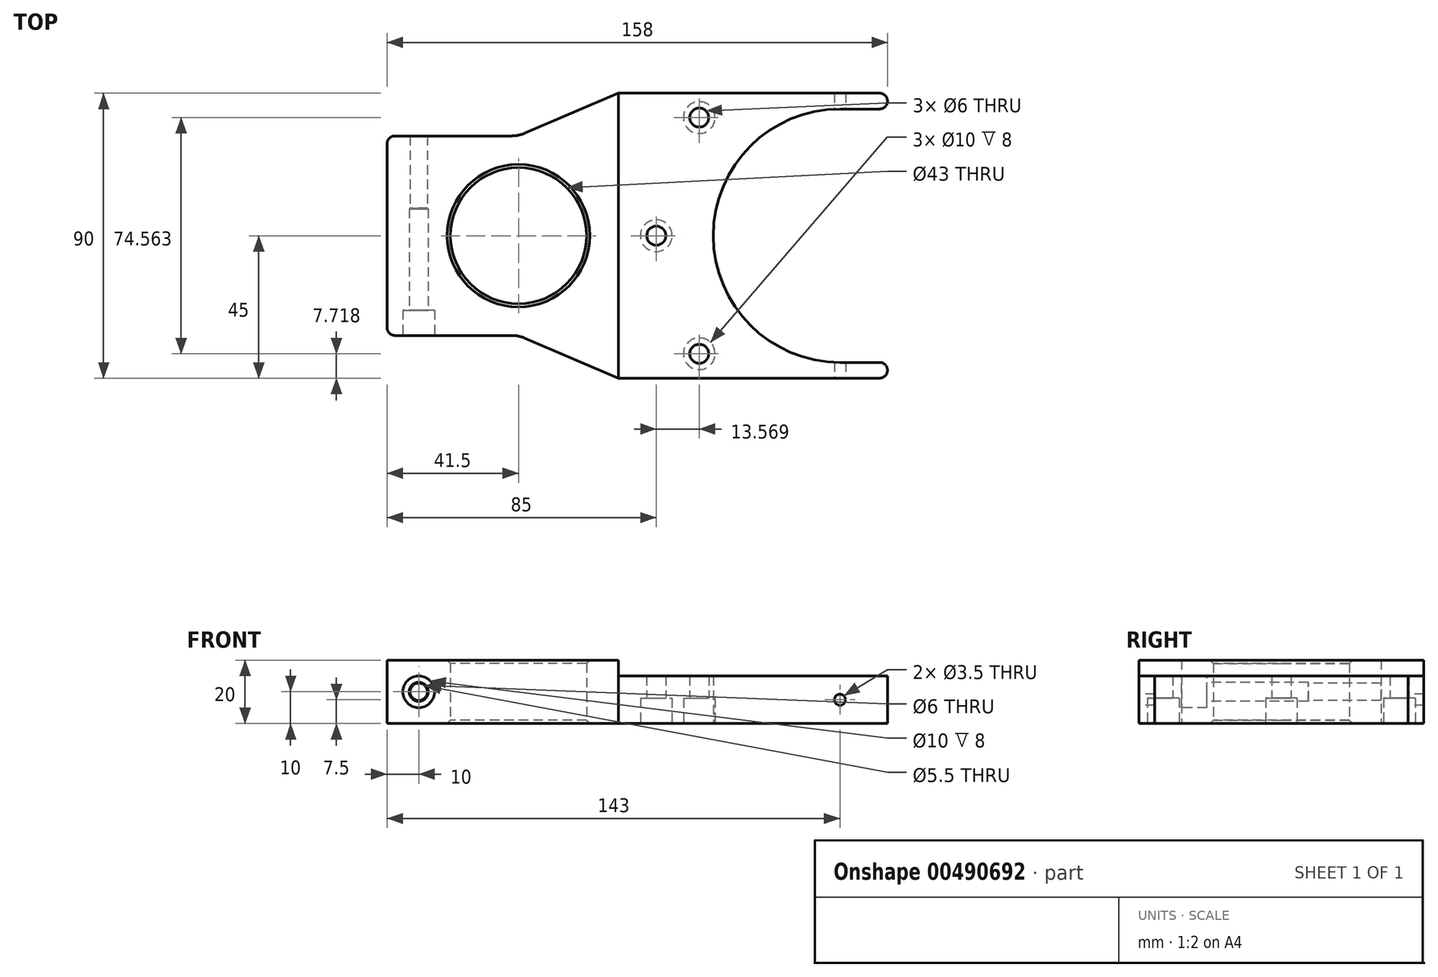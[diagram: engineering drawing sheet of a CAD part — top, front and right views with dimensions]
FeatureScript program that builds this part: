
annotation { "Feature Type Name" : "Feature", "Feature Type Description" : "" }
export const myFeature = defineFeature(function(context is Context, id is Id, definition is map)
    precondition{}
    {
        {
            var Q0;
            Q0=qCreatedBy(makeId("Top.planeOp"),FACE);
            var sketch = newSketch(context, id + "F0", { "sketchPlane" : qUnion([Q0])});
            skCircle(sketch, "E0", {"center": v(0, 0) * mm, "radius": 21.5 * mm});
            skLineSegment(sketch, "E1", {"start": v(0, 0) * mm, "end": v(101.5, 0) * mm, "construction": true});
            skCircle(sketch, "E2", {"center": v(101.5, 0) * mm, "radius": 40 * mm});
            skCircle(sketch, "E3", {"center": v(0, 0) * mm, "radius": 31.5 * mm, "construction": true});
            skCircle(sketch, "E4", {"center": v(101.5, 0) * mm, "radius": 45 * mm, "construction": true});
            skLineSegment(sketch, "E5.bottom", {"start": v(0, 31.5) * mm, "end": v(-31.5, 31.5) * mm});
            skLineSegment(sketch, "E5.top", {"start": v(0, -31.5) * mm, "end": v(-31.5, -31.5) * mm});
            skLineSegment(sketch, "E5.left", {"start": v(0, 31.5) * mm, "end": v(0, -31.5) * mm});
            skLineSegment(sketch, "E5.right", {"start": v(-31.5, 31.5) * mm, "end": v(-31.5, -31.5) * mm});
            skLineSegment(sketch, "E6", {"start": v(101.5, 45) * mm, "end": v(101.5, -45) * mm});
            skLineSegment(sketch, "E7", {"start": v(31.5, 45) * mm, "end": v(31.5, -45) * mm});
            skLineSegment(sketch, "E8", {"start": v(101.5, 45) * mm, "end": v(31.5, 45) * mm});
            skLineSegment(sketch, "E9", {"start": v(101.5, -45) * mm, "end": v(31.5, -45) * mm});
            skLineSegment(sketch, "E10", {"start": v(31.5, 45) * mm, "end": v(0, 31.5) * mm});
            skLineSegment(sketch, "E11", {"start": v(31.5, -45) * mm, "end": v(0, -31.5) * mm});
            skCircle(sketch, "E12", {"center": v(101.5, 0) * mm, "radius": 58 * mm, "construction": true});
            skPoint(sketch, "E13", {"position": v(43.5, 0) * mm});
            skPoint(sketch, "E14", {"position": v(57.07, 37.28) * mm});
            skPoint(sketch, "E15", {"position": v(57.07, -37.28) * mm});
            skLineSegment(sketch, "E16", {"start": v(57.07, 37.28) * mm, "end": v(101.5, 0) * mm, "construction": true});
            skLineSegment(sketch, "E17", {"start": v(57.07, -37.28) * mm, "end": v(101.5, 0) * mm, "construction": true});
            skLineSegment(sketch, "E18.bottom", {"start": v(101.5, 45) * mm, "end": v(116.5, 45) * mm});
            skLineSegment(sketch, "E18.top", {"start": v(101.5, 40) * mm, "end": v(116.5, 40) * mm});
            skLineSegment(sketch, "E18.left", {"start": v(101.5, 45) * mm, "end": v(101.5, 40) * mm});
            skLineSegment(sketch, "E18.right", {"start": v(116.5, 45) * mm, "end": v(116.5, 40) * mm});
            skLineSegment(sketch, "E19.bottom", {"start": v(101.5, -45) * mm, "end": v(116.5, -45) * mm});
            skLineSegment(sketch, "E19.top", {"start": v(101.5, -40) * mm, "end": v(116.5, -40) * mm});
            skLineSegment(sketch, "E19.left", {"start": v(101.5, -45) * mm, "end": v(101.5, -40) * mm});
            skLineSegment(sketch, "E19.right", {"start": v(116.5, -45) * mm, "end": v(116.5, -40) * mm});
            skLineSegment(sketch, "E20.bottom", {"start": v(-31.5, 31.5) * mm, "end": v(-41.5, 31.5) * mm});
            skLineSegment(sketch, "E20.top", {"start": v(-31.5, -31.5) * mm, "end": v(-41.5, -31.5) * mm});
            skLineSegment(sketch, "E20.right", {"start": v(-41.5, 31.5) * mm, "end": v(-41.5, -31.5) * mm});
            skSolve(sketch);
        }
        {
            var Q0;
            {var subQ1=sQuery(id+"F0.wireOp",EDGE,"E5.bottom");Q0=makeQuery(id+"F0.imprint","IMPRINT",FACE,{"disambiguationData":[TD([[makeQuery(id+"F0.imprint","IMPRINT",EDGE,{"derivedFrom":subQ1}),1.0]])]});}
            var Q1;
            Q1=makeQuery(id+"F0.imprint","IMPRINT",FACE,{"disambiguationData":[TD([[makeQuery(id+"F0.imprint","IMPRINT",EDGE,{"derivedFrom":sQuery(id+"F0.wireOp",EDGE,"E7")}),-1.0]])]});
            var Q2;
            Q2=makeQuery(id+"F0.imprint","IMPRINT",FACE,{"disambiguationData":[TD([[makeQuery(id+"F0.imprint","IMPRINT",EDGE,{"derivedFrom":sQuery(id+"F0.wireOp",EDGE,"E20.bottom")}),1.0]])]});
            extrude(context, id + "F1", {"entities" : qUnion([Q0, Q1, Q2]), "depth" : 20 * mm});
        }
        {
            var Q0;
            Q0=makeQuery(id+"F0.imprint","IMPRINT",FACE,{"disambiguationData":[TD([[makeQuery(id+"F0.imprint","IMPRINT",EDGE,{"derivedFrom":sQuery(id+"F0.wireOp",EDGE,"E7")}),1.0]])]});
            var Q1;
            Q1=makeQuery(id+"F0.imprint","IMPRINT",FACE,{"disambiguationData":[TD([[makeQuery(id+"F0.imprint","IMPRINT",EDGE,{"derivedFrom":sQuery(id+"F0.wireOp",EDGE,"E19.bottom")}),1.0]])]});
            var Q2;
            Q2=makeQuery(id+"F0.imprint","IMPRINT",FACE,{"disambiguationData":[TD([[makeQuery(id+"F0.imprint","IMPRINT",EDGE,{"derivedFrom":sQuery(id+"F0.wireOp",EDGE,"E18.bottom")}),-1.0]])]});
            extrude(context, id + "F2", {"entities" : qUnion([Q0, Q1, Q2]), "operationType" : NewBodyOperationType.ADD, "depth" : 15 * mm});
        }
        {
            var Q0;
            Q0=sQuery(id+"F0.wireOp",VERTEX,"E15");
            var Q1;
            Q1=sQuery(id+"F0.wireOp",VERTEX,"E13");
            var Q2;
            Q2=sQuery(id+"F0.wireOp",VERTEX,"E14");
            var Q3;
            Q3=makeQuery(id+"F1.opExtrude","SWEPT_BODY",BODY,{"disambiguationData":[OSD([sQuery(id+"F0.wireOp",EDGE,"E0"),sQuery(id+"F0.wireOp",EDGE,"E2"),sQuery(id+"F0.wireOp",EDGE,"E5.bottom"),sQuery(id+"F0.wireOp",EDGE,"E5.top"),sQuery(id+"F0.wireOp",EDGE,"E5.right"),sQuery(id+"F0.wireOp",EDGE,"E8"),sQuery(id+"F0.wireOp",EDGE,"E9"),sQuery(id+"F0.wireOp",EDGE,"E10"),sQuery(id+"F0.wireOp",EDGE,"E11"),sQuery(id+"F0.wireOp",EDGE,"E18.left"),sQuery(id+"F0.wireOp",EDGE,"E19.left")])]});
            hole(context, id + "F3", {"style" : HoleStyle.C_BORE, "endStyle" : HoleEndStyle.THROUGH, "oppositeDirection" : true, "holeDiameter" : 6 * mm, "cBoreDiameter" : 10 * mm, "cBoreDepth" : 8 * mm, "isTappedThrough" : true, "tappedDepth" : 12 * mm, "tapClearance" : 3, "startFromSketch" : true, "locations" : qUnion([Q0, Q1, Q2]), "scope" : qUnion([Q3])});
        }
        {
            var Q0;
            Q0=makeQuery(id+"F1.opExtrude","SWEPT_EDGE",EDGE,{"disambiguationData":[OSD([sQuery(id+"F0.wireOp",EDGE,"E5.bottom"),sQuery(id+"F0.wireOp",EDGE,"E5.left"),sQuery(id+"F0.wireOp",EDGE,"E10")])]});
            var Q1;
            Q1=makeQuery(id+"F1.opExtrude","SWEPT_EDGE",EDGE,{"disambiguationData":[OSD([sQuery(id+"F0.wireOp",EDGE,"E5.top"),sQuery(id+"F0.wireOp",EDGE,"E5.left"),sQuery(id+"F0.wireOp",EDGE,"E11")])]});
            fillet(context, id + "F4", {"entities" : qUnion([Q0, Q1]), "radius" : 10 * mm, "tangentPropagation" : true, "allowEdgeOverflow" : false});
        }
        {
            var Q0;
            Q0=makeQuery(id+"F1.opExtrude","SWEPT_EDGE",EDGE,{"disambiguationData":[OSD([sQuery(id+"F0.wireOp",EDGE,"E5.top"),sQuery(id+"F0.wireOp",EDGE,"E5.right")])]});
            var Q1;
            Q1=makeQuery(id+"F1.opExtrude","SWEPT_EDGE",EDGE,{"disambiguationData":[OSD([sQuery(id+"F0.wireOp",EDGE,"E5.bottom"),sQuery(id+"F0.wireOp",EDGE,"E5.right")])]});
            var Q2;
            Q2=makeQuery(id+"F1.opExtrude","SWEPT_EDGE",EDGE,{"disambiguationData":[OSD([sQuery(id+"F0.wireOp",EDGE,"E2"),sQuery(id+"F0.wireOp",EDGE,"E6"),sQuery(id+"F0.wireOp",EDGE,"E19.top"),sQuery(id+"F0.wireOp",EDGE,"E19.left")])]});
            var Q3;
            Q3=makeQuery(id+"F1.opExtrude","SWEPT_EDGE",EDGE,{"disambiguationData":[OSD([sQuery(id+"F0.wireOp",EDGE,"E2"),sQuery(id+"F0.wireOp",EDGE,"E6"),sQuery(id+"F0.wireOp",EDGE,"E18.top"),sQuery(id+"F0.wireOp",EDGE,"E18.left")])]});
            var Q4;
            Q4=makeQuery(id+"F1.opExtrude","SWEPT_EDGE",EDGE,{"disambiguationData":[OSD([sQuery(id+"F0.wireOp",EDGE,"E20.top"),sQuery(id+"F0.wireOp",EDGE,"E20.right")])]});
            var Q5;
            Q5=makeQuery(id+"F1.opExtrude","SWEPT_EDGE",EDGE,{"disambiguationData":[OSD([sQuery(id+"F0.wireOp",EDGE,"E20.bottom"),sQuery(id+"F0.wireOp",EDGE,"E20.right")])]});
            var Q6;
            Q6=makeQuery(id+"F1.opExtrude","SWEPT_EDGE",EDGE,{"disambiguationData":[OSD([sQuery(id+"F0.wireOp",EDGE,"E18.top"),sQuery(id+"F0.wireOp",EDGE,"E18.right")])]});
            var Q7;
            Q7=makeQuery(id+"F1.opExtrude","SWEPT_EDGE",EDGE,{"disambiguationData":[OSD([sQuery(id+"F0.wireOp",EDGE,"E19.top"),sQuery(id+"F0.wireOp",EDGE,"E19.right")])]});
            var Q8;
            Q8=makeQuery(id+"F2.opExtrude","SWEPT_EDGE",EDGE,{"disambiguationData":[OSD([sQuery(id+"F0.wireOp",EDGE,"E19.bottom"),sQuery(id+"F0.wireOp",EDGE,"E19.right")])]});
            var Q9;
            Q9=makeQuery(id+"F2.opExtrude","SWEPT_EDGE",EDGE,{"disambiguationData":[OSD([sQuery(id+"F0.wireOp",EDGE,"E19.top"),sQuery(id+"F0.wireOp",EDGE,"E19.right")])]});
            var Q10;
            Q10=makeQuery(id+"F2.opExtrude","SWEPT_EDGE",EDGE,{"disambiguationData":[OSD([sQuery(id+"F0.wireOp",EDGE,"E18.top"),sQuery(id+"F0.wireOp",EDGE,"E18.right")])]});
            var Q11;
            Q11=makeQuery(id+"F2.opExtrude","SWEPT_EDGE",EDGE,{"disambiguationData":[OSD([sQuery(id+"F0.wireOp",EDGE,"E18.bottom"),sQuery(id+"F0.wireOp",EDGE,"E18.right")])]});
            fillet(context, id + "F5", {"entities" : qUnion([Q0, Q1, Q2, Q3, Q4, Q5, Q6, Q7, Q8, Q9, Q10, Q11]), "radius" : 2.5 * mm, "tangentPropagation" : true, "allowEdgeOverflow" : false});
        }
        {
            var Q0;
            Q0=makeQuery(id+"F1.opExtrude","CAP_EDGE",EDGE,{"disambiguationData":[OSD([sQuery(id+"F0.wireOp",EDGE,"E0")])],"isStart":false});
            var Q1;
            Q1=makeQuery(id+"F1.opExtrude","CAP_EDGE",EDGE,{"disambiguationData":[OSD([sQuery(id+"F0.wireOp",EDGE,"E0")])],"isStart":true});
            chamfer(context, id + "F6", {"entities" : qUnion([Q0, Q1]), "width" : 1 * mm, "tangentPropagation" : true});
        }
        {
            var Q0;
            Q0=makeQuery(id+"F1.opExtrude","SWEPT_FACE",FACE,{"disambiguationData":[OSD([sQuery(id+"F0.wireOp",EDGE,"E5.top"),sQuery(id+"F0.wireOp",EDGE,"E20.top")])]});
            var sketch = newSketch(context, id + "F7", { "sketchPlane" : qUnion([Q0])});
            skLineSegment(sketch, "E21", {"start": v(-39, 10) * mm, "end": v(-2.05, 10) * mm, "construction": true});
            skPoint(sketch, "E22", {"position": v(-31.5, 10) * mm});
            skSolve(sketch);
        }
        {
            var Q0;
            Q0=sQuery(id+"F7.wireOp",VERTEX,"E22");
            var Q1;
            Q1=makeQuery(id+"F1.opExtrude","SWEPT_BODY",BODY,{"disambiguationData":[OSD([sQuery(id+"F0.wireOp",EDGE,"E0"),sQuery(id+"F0.wireOp",EDGE,"E2"),sQuery(id+"F0.wireOp",EDGE,"E5.bottom"),sQuery(id+"F0.wireOp",EDGE,"E5.top"),sQuery(id+"F0.wireOp",EDGE,"E8"),sQuery(id+"F0.wireOp",EDGE,"E9"),sQuery(id+"F0.wireOp",EDGE,"E10"),sQuery(id+"F0.wireOp",EDGE,"E11"),sQuery(id+"F0.wireOp",EDGE,"E18.bottom"),sQuery(id+"F0.wireOp",EDGE,"E18.top"),sQuery(id+"F0.wireOp",EDGE,"E18.right"),sQuery(id+"F0.wireOp",EDGE,"E19.bottom"),sQuery(id+"F0.wireOp",EDGE,"E19.top"),sQuery(id+"F0.wireOp",EDGE,"E19.right"),sQuery(id+"F0.wireOp",EDGE,"E20.bottom"),sQuery(id+"F0.wireOp",EDGE,"E20.top"),sQuery(id+"F0.wireOp",EDGE,"E20.right")])]});
            hole(context, id + "F8", {"style" : HoleStyle.C_BORE, "endStyle" : HoleEndStyle.BLIND, "holeDiameter" : 6 * mm, "cBoreDiameter" : 10 * mm, "cBoreDepth" : 8 * mm, "holeDepth" : 40 * mm, "isTappedThrough" : true, "tappedDepth" : 12 * mm, "tapClearance" : 3, "startFromSketch" : true, "locations" : qUnion([Q0]), "scope" : qUnion([Q1])});
        }
        {
            var Q0;
            Q0=sQuery(id+"F7.wireOp",VERTEX,"E22");
            var Q1;
            Q1=makeQuery(id+"F1.opExtrude","SWEPT_BODY",BODY,{"disambiguationData":[OSD([sQuery(id+"F0.wireOp",EDGE,"E0"),sQuery(id+"F0.wireOp",EDGE,"E2"),sQuery(id+"F0.wireOp",EDGE,"E5.bottom"),sQuery(id+"F0.wireOp",EDGE,"E5.top"),sQuery(id+"F0.wireOp",EDGE,"E8"),sQuery(id+"F0.wireOp",EDGE,"E9"),sQuery(id+"F0.wireOp",EDGE,"E10"),sQuery(id+"F0.wireOp",EDGE,"E11"),sQuery(id+"F0.wireOp",EDGE,"E18.bottom"),sQuery(id+"F0.wireOp",EDGE,"E18.top"),sQuery(id+"F0.wireOp",EDGE,"E18.right"),sQuery(id+"F0.wireOp",EDGE,"E19.bottom"),sQuery(id+"F0.wireOp",EDGE,"E19.top"),sQuery(id+"F0.wireOp",EDGE,"E19.right"),sQuery(id+"F0.wireOp",EDGE,"E20.bottom"),sQuery(id+"F0.wireOp",EDGE,"E20.top"),sQuery(id+"F0.wireOp",EDGE,"E20.right")])]});
            hole(context, id + "F9", {"style" : HoleStyle.SIMPLE, "endStyle" : HoleEndStyle.THROUGH, "holeDiameter" : 5.5 * mm, "isTappedThrough" : true, "tappedDepth" : 12 * mm, "tapClearance" : 3, "startFromSketch" : true, "locations" : qUnion([Q0]), "scope" : qUnion([Q1])});
        }
        {
            var Q0;
            Q0=makeQuery(id+"F2.opExtrude","SWEPT_FACE",FACE,{"disambiguationData":[OSD([sQuery(id+"F0.wireOp",EDGE,"E9"),sQuery(id+"F0.wireOp",EDGE,"E19.bottom")])]});
            var sketch = newSketch(context, id + "F10", { "sketchPlane" : qUnion([Q0])});
            skLineSegment(sketch, "E23", {"start": v(114, 7.5) * mm, "end": v(31.5, 7.5) * mm, "construction": true});
            skPoint(sketch, "E24", {"position": v(101.5, 7.5) * mm});
            skSolve(sketch);
        }
        {
            var Q0;
            Q0=sQuery(id+"F10.wireOp",VERTEX,"E24");
            var Q1;
            Q1=makeQuery(id+"F1.opExtrude","SWEPT_BODY",BODY,{"disambiguationData":[OSD([sQuery(id+"F0.wireOp",EDGE,"E0"),sQuery(id+"F0.wireOp",EDGE,"E2"),sQuery(id+"F0.wireOp",EDGE,"E5.bottom"),sQuery(id+"F0.wireOp",EDGE,"E5.top"),sQuery(id+"F0.wireOp",EDGE,"E8"),sQuery(id+"F0.wireOp",EDGE,"E9"),sQuery(id+"F0.wireOp",EDGE,"E10"),sQuery(id+"F0.wireOp",EDGE,"E11"),sQuery(id+"F0.wireOp",EDGE,"E18.bottom"),sQuery(id+"F0.wireOp",EDGE,"E18.top"),sQuery(id+"F0.wireOp",EDGE,"E18.right"),sQuery(id+"F0.wireOp",EDGE,"E19.bottom"),sQuery(id+"F0.wireOp",EDGE,"E19.top"),sQuery(id+"F0.wireOp",EDGE,"E19.right"),sQuery(id+"F0.wireOp",EDGE,"E20.bottom"),sQuery(id+"F0.wireOp",EDGE,"E20.top"),sQuery(id+"F0.wireOp",EDGE,"E20.right")])]});
            hole(context, id + "F11", {"style" : HoleStyle.SIMPLE, "endStyle" : HoleEndStyle.THROUGH, "holeDiameter" : 3.5 * mm, "isTappedThrough" : true, "tappedDepth" : 12 * mm, "tapClearance" : 3, "startFromSketch" : true, "locations" : qUnion([Q0]), "scope" : qUnion([Q1])});
        }
    });
